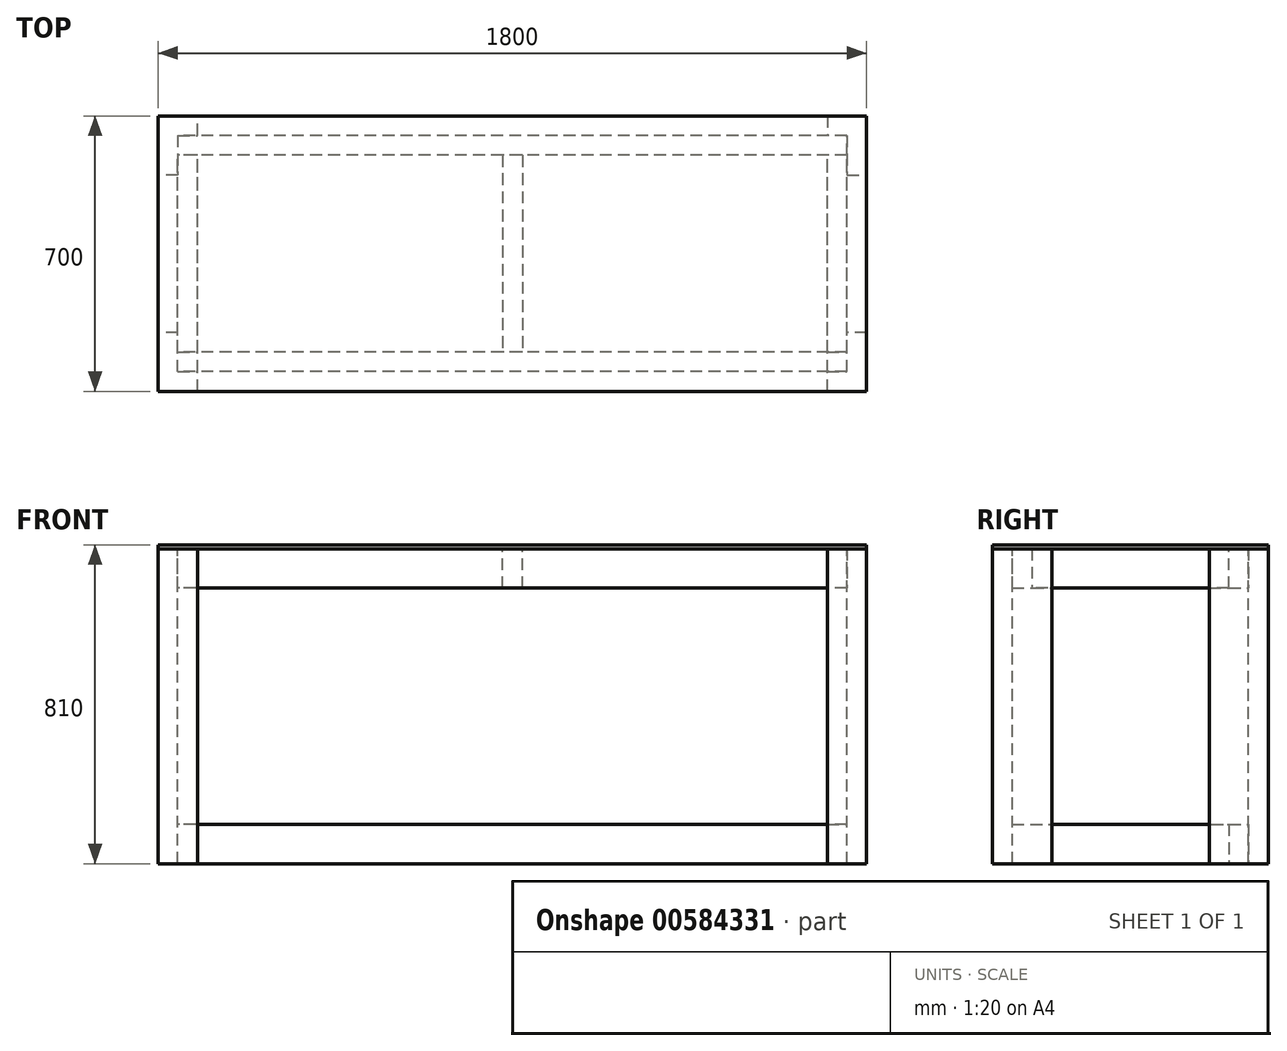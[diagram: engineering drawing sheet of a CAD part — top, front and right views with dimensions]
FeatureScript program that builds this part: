
annotation { "Feature Type Name" : "Feature", "Feature Type Description" : "" }
export const myFeature = defineFeature(function(context is Context, id is Id, definition is map)
    precondition{}
    {
        {
            var Q0;
            Q0=qCreatedBy(makeId("Top.planeOp"),FACE);
            var sketch = newSketch(context, id + "F0", { "sketchPlane" : qUnion([Q0])});
            skLineSegment(sketch, "E0.bottom", {"start": v(-900, 350) * mm, "end": v(900, 350) * mm});
            skLineSegment(sketch, "E0.top", {"start": v(-900, -350) * mm, "end": v(900, -350) * mm});
            skLineSegment(sketch, "E0.left", {"start": v(-900, 350) * mm, "end": v(-900, -350) * mm});
            skLineSegment(sketch, "E0.right", {"start": v(900, 350) * mm, "end": v(900, -350) * mm});
            skPoint(sketch, "E0.middle", {"position": v(0, 0) * mm});
            skSolve(sketch);
        }
        {
            var Q0;
            Q0 = qSketchRegion(id + "F0", true);
            extrude(context, id + "F1", {"entities" : qUnion([Q0]), "depth" : 10 * mm, "offsetDistance" : 25 * mm});
        }
        {
            var Q0;
            Q0=makeQuery(id+"F1.opExtrude","CAP_FACE",FACE,{"disambiguationData":[OSD([sQuery(id+"F0.wireOp",EDGE,"E0.bottom"),sQuery(id+"F0.wireOp",EDGE,"E0.top"),sQuery(id+"F0.wireOp",EDGE,"E0.left"),sQuery(id+"F0.wireOp",EDGE,"E0.right")])],"isStart":true});
            var sketch = newSketch(context, id + "F2", { "sketchPlane" : qUnion([Q0])});
            skLineSegment(sketch, "E1.bottom", {"start": v(-900, 350) * mm, "end": v(-800, 350) * mm});
            skLineSegment(sketch, "E1.top", {"start": v(-900, 300) * mm, "end": v(-800, 300) * mm});
            skLineSegment(sketch, "E1.left", {"start": v(-900, 350) * mm, "end": v(-900, 300) * mm});
            skLineSegment(sketch, "E1.right", {"start": v(-800, 350) * mm, "end": v(-800, 300) * mm});
            skLineSegment(sketch, "E2.bottom", {"start": v(-850, 300) * mm, "end": v(-900, 300) * mm});
            skLineSegment(sketch, "E2.top", {"start": v(-850, 200) * mm, "end": v(-900, 200) * mm});
            skLineSegment(sketch, "E2.left", {"start": v(-850, 300) * mm, "end": v(-850, 200) * mm});
            skLineSegment(sketch, "E2.right", {"start": v(-900, 300) * mm, "end": v(-900, 200) * mm});
            skLineSegment(sketch, "E3.bottom", {"start": v(-900, -300) * mm, "end": v(-800, -300) * mm});
            skLineSegment(sketch, "E3.top", {"start": v(-900, -350) * mm, "end": v(-800, -350) * mm});
            skLineSegment(sketch, "E3.left", {"start": v(-900, -300) * mm, "end": v(-900, -350) * mm});
            skLineSegment(sketch, "E3.right", {"start": v(-800, -300) * mm, "end": v(-800, -350) * mm});
            skLineSegment(sketch, "E4.bottom", {"start": v(-850, -300) * mm, "end": v(-900, -300) * mm});
            skLineSegment(sketch, "E4.top", {"start": v(-850, -200) * mm, "end": v(-900, -200) * mm});
            skLineSegment(sketch, "E4.left", {"start": v(-850, -300) * mm, "end": v(-850, -200) * mm});
            skLineSegment(sketch, "E4.right", {"start": v(-900, -300) * mm, "end": v(-900, -200) * mm});
            skLineSegment(sketch, "E5.bottom", {"start": v(900, -350) * mm, "end": v(800, -350) * mm});
            skLineSegment(sketch, "E5.top", {"start": v(900, -300) * mm, "end": v(800, -300) * mm});
            skLineSegment(sketch, "E5.left", {"start": v(900, -350) * mm, "end": v(900, -300) * mm});
            skLineSegment(sketch, "E5.right", {"start": v(800, -350) * mm, "end": v(800, -300) * mm});
            skLineSegment(sketch, "E6.bottom", {"start": v(850, -300) * mm, "end": v(900, -300) * mm});
            skLineSegment(sketch, "E6.top", {"start": v(850, -200) * mm, "end": v(900, -200) * mm});
            skLineSegment(sketch, "E6.left", {"start": v(850, -300) * mm, "end": v(850, -200) * mm});
            skLineSegment(sketch, "E6.right", {"start": v(900, -300) * mm, "end": v(900, -200) * mm});
            skLineSegment(sketch, "E7.bottom", {"start": v(900, 350) * mm, "end": v(800, 350) * mm});
            skLineSegment(sketch, "E7.top", {"start": v(900, 300) * mm, "end": v(800, 300) * mm});
            skLineSegment(sketch, "E7.left", {"start": v(900, 350) * mm, "end": v(900, 300) * mm});
            skLineSegment(sketch, "E7.right", {"start": v(800, 350) * mm, "end": v(800, 300) * mm});
            skPoint(sketch, "E8.oppositeSnap0", {"position": v(850, 300) * mm});
            skLineSegment(sketch, "E8.bottom", {"start": v(900, 300) * mm, "end": v(850, 300) * mm});
            skLineSegment(sketch, "E8.top", {"start": v(900, 200) * mm, "end": v(850, 200) * mm});
            skLineSegment(sketch, "E8.left", {"start": v(900, 300) * mm, "end": v(900, 200) * mm});
            skLineSegment(sketch, "E8.right", {"start": v(850, 300) * mm, "end": v(850, 200) * mm});
            skSolve(sketch);
        }
        {
            var Q0;
            Q0 = qSketchRegion(id + "F2", true);
            extrude(context, id + "F3", {"entities" : qUnion([Q0]), "depth" : 800 * mm, "offsetDistance" : 25 * mm});
        }
        {
            var Q0;
            Q0=makeQuery(id+"F3.opExtrude","SWEPT_FACE",FACE,{"disambiguationData":[OSD([sQuery(id+"F2.wireOp",EDGE,"E2.left")])]});
            var sketch = newSketch(context, id + "F4", { "sketchPlane" : qUnion([Q0])});
            skLineSegment(sketch, "E9.bottom", {"start": v(-300, 0) * mm, "end": v(-250, 0) * mm});
            skLineSegment(sketch, "E9.top", {"start": v(-300, -100) * mm, "end": v(-250, -100) * mm});
            skLineSegment(sketch, "E9.left", {"start": v(-300, 0) * mm, "end": v(-300, -100) * mm});
            skLineSegment(sketch, "E9.right", {"start": v(-250, 0) * mm, "end": v(-250, -100) * mm});
            skSolve(sketch);
        }
        {
            var Q0;
            Q0 = qSketchRegion(id + "F4", true);
            var Q1;
            Q1=makeQuery(id+"F3.opExtrude","SWEPT_FACE",FACE,{"disambiguationData":[OSD([sQuery(id+"F2.wireOp",EDGE,"E8.right")])]});
            extrude(context, id + "F5", {"entities" : qUnion([Q0]), "endBound" : BoundingType.UP_TO_SURFACE, "depth" : 25 * mm, "endBoundEntityFace" : qUnion([Q1]), "offsetDistance" : 25 * mm});
        }
        {
            var Q0;
            Q0=makeQuery(id+"F3.opExtrude","SWEPT_FACE",FACE,{"disambiguationData":[OSD([sQuery(id+"F2.wireOp",EDGE,"E4.left")])]});
            var sketch = newSketch(context, id + "F6", { "sketchPlane" : qUnion([Q0])});
            skLineSegment(sketch, "E10.bottom", {"start": v(300, 0) * mm, "end": v(250, 0) * mm});
            skLineSegment(sketch, "E10.top", {"start": v(300, -100) * mm, "end": v(250, -100) * mm});
            skLineSegment(sketch, "E10.left", {"start": v(300, 0) * mm, "end": v(300, -100) * mm});
            skLineSegment(sketch, "E10.right", {"start": v(250, 0) * mm, "end": v(250, -100) * mm});
            skSolve(sketch);
        }
        {
            var Q0;
            Q0 = qSketchRegion(id + "F6", true);
            var Q1;
            Q1=makeQuery(id+"F3.opExtrude","SWEPT_FACE",FACE,{"disambiguationData":[OSD([sQuery(id+"F2.wireOp",EDGE,"E6.left")])]});
            extrude(context, id + "F7", {"entities" : qUnion([Q0]), "endBound" : BoundingType.UP_TO_SURFACE, "depth" : 25 * mm, "endBoundEntityFace" : qUnion([Q1]), "offsetDistance" : 25 * mm});
        }
        {
            var Q0;
            Q0=makeQuery(id+"F7.opExtrude","SWEPT_FACE",FACE,{"disambiguationData":[OSD([sQuery(id+"F6.wireOp",EDGE,"E10.right")])]});
            var sketch = newSketch(context, id + "F8", { "sketchPlane" : qUnion([Q0])});
            skLineSegment(sketch, "E11.bottom", {"start": v(-850, 0) * mm, "end": v(-800, 0) * mm});
            skLineSegment(sketch, "E11.top", {"start": v(-850, -100) * mm, "end": v(-800, -100) * mm});
            skLineSegment(sketch, "E11.left", {"start": v(-850, 0) * mm, "end": v(-850, -100) * mm});
            skLineSegment(sketch, "E11.right", {"start": v(-800, 0) * mm, "end": v(-800, -100) * mm});
            skSolve(sketch);
        }
        {
            var Q0;
            Q0 = qSketchRegion(id + "F8", true);
            var Q1;
            Q1=makeQuery(id+"F5.opExtrude","SWEPT_FACE",FACE,{"disambiguationData":[OSD([sQuery(id+"F4.wireOp",EDGE,"E9.right")])]});
            extrude(context, id + "F9", {"entities" : qUnion([Q0]), "endBound" : BoundingType.UP_TO_SURFACE, "depth" : 25 * mm, "endBoundEntityFace" : qUnion([Q1]), "offsetDistance" : 25 * mm});
        }
        {
            var Q0;
            Q0=makeQuery(id+"F7.opExtrude","SWEPT_FACE",FACE,{"disambiguationData":[OSD([sQuery(id+"F6.wireOp",EDGE,"E10.right")])]});
            var sketch = newSketch(context, id + "F10", { "sketchPlane" : qUnion([Q0])});
            skLineSegment(sketch, "E12.bottom", {"start": v(850, 0) * mm, "end": v(800, 0) * mm});
            skLineSegment(sketch, "E12.top", {"start": v(850, -100) * mm, "end": v(800, -100) * mm});
            skLineSegment(sketch, "E12.left", {"start": v(850, 0) * mm, "end": v(850, -100) * mm});
            skLineSegment(sketch, "E12.right", {"start": v(800, 0) * mm, "end": v(800, -100) * mm});
            skSolve(sketch);
        }
        {
            var Q0;
            Q0 = qSketchRegion(id + "F10", true);
            var Q1;
            Q1=makeQuery(id+"F5.opExtrude","SWEPT_FACE",FACE,{"disambiguationData":[OSD([sQuery(id+"F4.wireOp",EDGE,"E9.right")])]});
            extrude(context, id + "F11", {"entities" : qUnion([Q0]), "endBound" : BoundingType.UP_TO_SURFACE, "depth" : 25 * mm, "endBoundEntityFace" : qUnion([Q1]), "offsetDistance" : 25 * mm});
        }
        {
            var Q0;
            Q0=makeQuery(id+"F3.opExtrude","SWEPT_FACE",FACE,{"disambiguationData":[OSD([sQuery(id+"F2.wireOp",EDGE,"E4.left")])]});
            var sketch = newSketch(context, id + "F12", { "sketchPlane" : qUnion([Q0])});
            skLineSegment(sketch, "E13.bottom", {"start": v(300, -800) * mm, "end": v(250, -800) * mm});
            skLineSegment(sketch, "E13.top", {"start": v(300, -700) * mm, "end": v(250, -700) * mm});
            skLineSegment(sketch, "E13.left", {"start": v(300, -800) * mm, "end": v(300, -700) * mm});
            skLineSegment(sketch, "E13.right", {"start": v(250, -800) * mm, "end": v(250, -700) * mm});
            skSolve(sketch);
        }
        {
            var Q0;
            Q0 = qSketchRegion(id + "F12", true);
            var Q1;
            Q1=makeQuery(id+"F3.opExtrude","SWEPT_FACE",FACE,{"disambiguationData":[OSD([sQuery(id+"F2.wireOp",EDGE,"E6.left")])]});
            extrude(context, id + "F13", {"entities" : qUnion([Q0]), "endBound" : BoundingType.UP_TO_SURFACE, "depth" : 25 * mm, "endBoundEntityFace" : qUnion([Q1]), "offsetDistance" : 25 * mm});
        }
        {
            var Q0;
            Q0=makeQuery(id+"F13.opExtrude","SWEPT_FACE",FACE,{"disambiguationData":[OSD([sQuery(id+"F12.wireOp",EDGE,"E13.right")])]});
            var sketch = newSketch(context, id + "F14", { "sketchPlane" : qUnion([Q0])});
            skLineSegment(sketch, "E14.bottom", {"start": v(850, -800) * mm, "end": v(800, -800) * mm});
            skLineSegment(sketch, "E14.top", {"start": v(850, -700) * mm, "end": v(800, -700) * mm});
            skLineSegment(sketch, "E14.left", {"start": v(850, -800) * mm, "end": v(850, -700) * mm});
            skLineSegment(sketch, "E14.right", {"start": v(800, -800) * mm, "end": v(800, -700) * mm});
            skSolve(sketch);
        }
        {
            var Q0;
            Q0 = qSketchRegion(id + "F14", true);
            var Q1;
            Q1=makeQuery(id+"F3.opExtrude","SWEPT_FACE",FACE,{"disambiguationData":[OSD([sQuery(id+"F2.wireOp",EDGE,"E7.top")])]});
            extrude(context, id + "F15", {"entities" : qUnion([Q0]), "endBound" : BoundingType.UP_TO_SURFACE, "depth" : 25 * mm, "endBoundEntityFace" : qUnion([Q1]), "offsetDistance" : 25 * mm});
        }
        {
            var Q0;
            Q0=makeQuery(id+"F13.opExtrude","SWEPT_FACE",FACE,{"disambiguationData":[OSD([sQuery(id+"F12.wireOp",EDGE,"E13.right")])]});
            var sketch = newSketch(context, id + "F16", { "sketchPlane" : qUnion([Q0])});
            skLineSegment(sketch, "E15.bottom", {"start": v(-850, -700) * mm, "end": v(-800, -700) * mm});
            skLineSegment(sketch, "E15.top", {"start": v(-850, -800) * mm, "end": v(-800, -800) * mm});
            skLineSegment(sketch, "E15.left", {"start": v(-850, -700) * mm, "end": v(-850, -800) * mm});
            skLineSegment(sketch, "E15.right", {"start": v(-800, -700) * mm, "end": v(-800, -800) * mm});
            skSolve(sketch);
        }
        {
            var Q0;
            Q0 = qSketchRegion(id + "F16", true);
            var Q1;
            Q1=makeQuery(id+"F3.opExtrude","SWEPT_FACE",FACE,{"disambiguationData":[OSD([sQuery(id+"F2.wireOp",EDGE,"E1.top")])]});
            extrude(context, id + "F17", {"entities" : qUnion([Q0]), "endBound" : BoundingType.UP_TO_SURFACE, "depth" : 25 * mm, "endBoundEntityFace" : qUnion([Q1]), "offsetDistance" : 25 * mm});
        }
        {
            var Q0;
            Q0=makeQuery(id+"F5.opExtrude","SWEPT_FACE",FACE,{"disambiguationData":[OSD([sQuery(id+"F4.wireOp",EDGE,"E9.right")])]});
            var sketch = newSketch(context, id + "F18", { "sketchPlane" : qUnion([Q0])});
            skLineSegment(sketch, "E16.bottom", {"start": v(0, -100) * mm, "end": v(-25, -100) * mm});
            skLineSegment(sketch, "E16.top", {"start": v(0, 0) * mm, "end": v(-25, 0) * mm});
            skLineSegment(sketch, "E16.left", {"start": v(0, -100) * mm, "end": v(0, 0) * mm});
            skLineSegment(sketch, "E16.right", {"start": v(-25, -100) * mm, "end": v(-25, 0) * mm});
            skLineSegment(sketch, "E17.bottom", {"start": v(0, -100) * mm, "end": v(25, -100) * mm});
            skLineSegment(sketch, "E17.top", {"start": v(0, 0) * mm, "end": v(25, 0) * mm});
            skLineSegment(sketch, "E17.right", {"start": v(25, -100) * mm, "end": v(25, 0) * mm});
            skSolve(sketch);
        }
        {
            var Q0;
            Q0 = qSketchRegion(id + "F18", true);
            var Q1;
            Q1=makeQuery(id+"F7.opExtrude","SWEPT_FACE",FACE,{"disambiguationData":[OSD([sQuery(id+"F6.wireOp",EDGE,"E10.right")])]});
            extrude(context, id + "F19", {"entities" : qUnion([Q0]), "endBound" : BoundingType.UP_TO_SURFACE, "depth" : 25 * mm, "endBoundEntityFace" : qUnion([Q1]), "offsetDistance" : 25 * mm});
        }
    });
